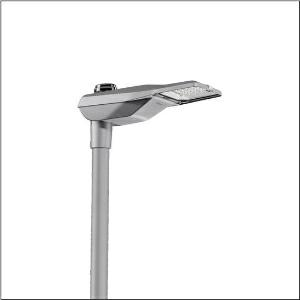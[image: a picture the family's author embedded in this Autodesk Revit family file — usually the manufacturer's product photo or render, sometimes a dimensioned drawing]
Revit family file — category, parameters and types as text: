
# Revit family: streetlight_sl_21_micro___stw1_0a_5xe5e47n08cb_41ee
name_source: partatom
category: Lighting Fixtures
units: mm (PartAtom-declared; Revit-internal decimal feet)

## family parameters
Cut with Voids When Loaded = No
Host = Face
Light Source = No
Part Type = Normal
Room Calculation Point = No
Round Connector Dimension = Use Diameter
Shared = No

## types (1)
- --- (1 x LED, 2380 lm, 15.8 W, 4000K)
    Apparent Load = 16 VA
    CIE Flux Codes = 38 75 98 100 100
    Color Rendering = 70
    Color Temperature = 4000K
    Default Elevation = 1800 mm
    Description = Streetlight SL 21 micro, mast luminaire, primary light control with lens, of PMMA, primary optical cover: cover, of toughened safety glass, transparent, light distribution: STW1.0a, light emission: direct distribution, primary light characteristic: asymmetric, installation type: post-top, LED, 3G 1.5mm², High Power LED, rated luminous flux: 2.380lm, luminous efficacy: 151lm/W, light colour: 740, colour temperature: 4000K, control: overheat protection, presetting dimming linear, constant luminous flux control, time-dependent luminous flux control, flexible luminous flux parameterisation, mains connection: 230..240V, AC, 50/60Hz, connection cable pre-assembled, cable length: 6,5m, wiring characteristics: H07RN-F, start of lifetime: 16W, end of service life: 16W, reduction: 8W, luminaire housing, of diecast aluminium (EN AC-44300), powder-coated, Siteco® metallic grey (DB 702S), corrosivity category C5 mid according to DIN EN ISO 12944, multi-level sealing system, sealing non-destructively replaceable, inclination adjustable: 0°, 5°, 10°, 15°, length: 528mm, width: 235mm, height: 110mm, spigot size: 76/60mm (post-top), protection rating (complete): IP66, insulation class (complete): insulation class I (protective earthing), certification: CE, ENEC, ENEC+, VDE, impact resistance: IK09, permissible operating ambient temperature for outdoor applications: -40..+50°C, standard-compliant lighting for roads and squares, packaging unit: 1 piece

Light Distribution: STW1.0a
    Height = 110 mm
    Lamp = 1 x LED
    Lamp Light Flux = 2380 lm
    Lamp Power = 15.8 W
    Lamp count = 1
    Length = 528 mm
    Luminous efficacy = 151 lm/W
    Manufacturer = Siteco
    ModVariant = No
    Model = 5XE5E47N08CB
    Number of Poles = 1
    OnlyDefault = Yes
    Power Factor = 1
    Product Name = Streetlight SL 21 micro | STW1.0a
    Product group = mast luminaire | pylon top
    ProductGroupID = 6100
    Protection Class = Protection class I
    Protection Degree = IP 66
    RLX_Detail_Level = 1
    RLX_Emergency_Light_Flux = 0 lm
    RLX_Emergency_Type = 0
    RLX_Emergency_Type_DB = No
    RlxData = <blob elided: 98293 chars, md5=094c863f>
    Socket = socket
    Standby Power = 0 W
    System Light Flux = 2380 lm
    System Power = 16 W
    Type Comments = factory setting: luminous flux: 100 % | dim-lin: 254 | 300 mA
    Type Image = l_1294375.jpg
    URL = http://relux.com
    VarID = @adj_085169
    Voltage = 0 V
    Weight = 0.00 kg
    Width = 235 mm

## geometry (parser evidence)
native form markers: Blend x4, Sweep x9
no freeform markers — native parametric forms only
